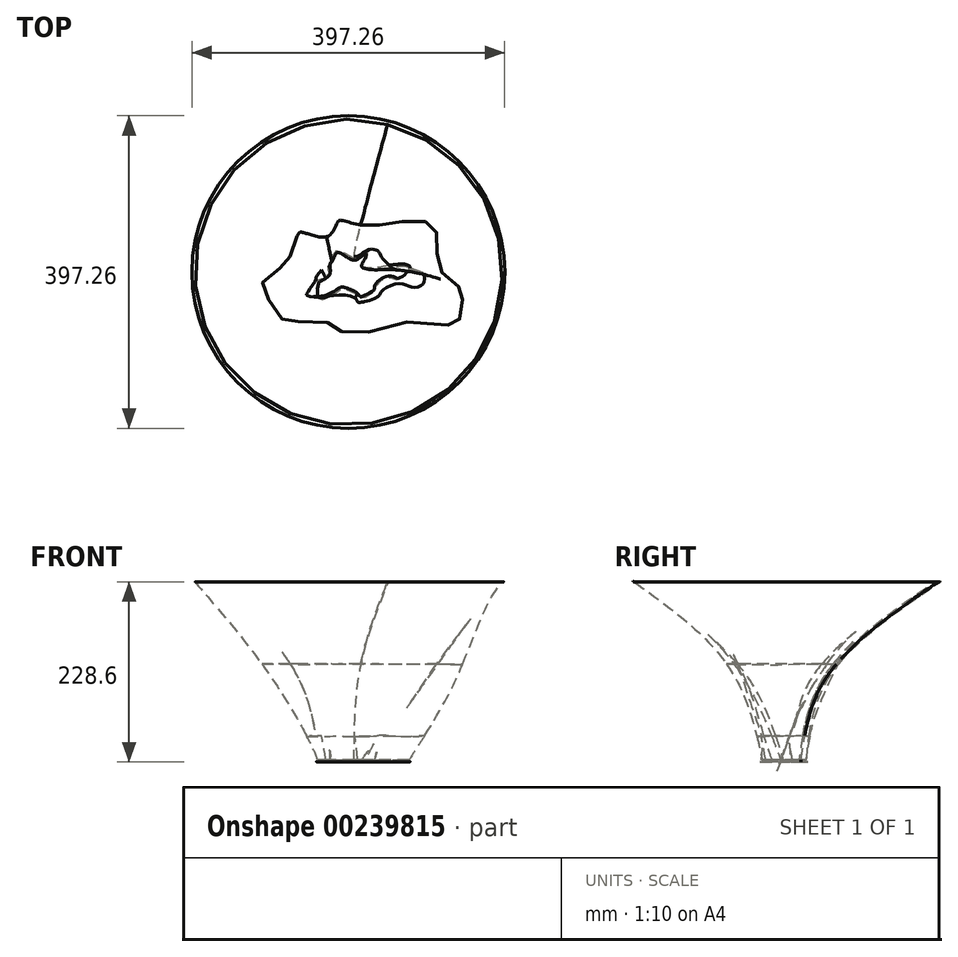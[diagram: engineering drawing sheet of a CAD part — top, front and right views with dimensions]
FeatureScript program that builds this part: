
annotation { "Feature Type Name" : "Feature", "Feature Type Description" : "" }
export const myFeature = defineFeature(function(context is Context, id is Id, definition is map)
    precondition{}
    {
        {
            var Q0;
            Q0=qCreatedBy(makeId("Top.planeOp"),FACE);
            var sketch = newSketch(context, id + "F0", { "sketchPlane" : qUnion([Q0])});
            skFitSpline(sketch, "E0", {"points": [v(14.79, 34.81) * mm, v(-29.61, 53.97) * mm, v(-52.04, 8.17) * mm, v(-46.44, 0) * mm, v(-67, -17.53) * mm, v(-77.75, -23.14) * mm, v(-80.55, -62.4) * mm, v(-67.47, -70.81) * mm, v(-22.6, -45.58) * mm, v(-13.72, -41.84) * mm, v(22.73, -59.6) * mm, v(26.94, -67.54) * mm, v(70.4, -45.1) * mm, v(70.4, -34.36) * mm, v(103.59, -13.33) * mm, v(124.62, -19.4) * mm, v(156.87, 8.17) * mm, v(145.18, 19.39) * mm, v(80.69, 12.38) * mm, v(69.47, 10.04) * mm, v(36.75, 13.31) * mm, v(39.1, 21.26) * mm, v(48.44, 46.96) * mm, v(40.5, 51.64) * mm, v(14.79, 34.81) * mm]});
            skSolve(sketch);
        }
        {
            var Q0;
            Q0=qCreatedBy(makeId("Top.planeOp"),FACE);
            cPlane(context, id + "F1", {"entities" : qUnion([Q0]), "cplaneType" : CPlaneType.OFFSET, "offset" : 203.2 * mm, "width" : 152.4 * mm, "height" : 152.4 * mm});
        }
        {
            var Q0;
            Q0=qCreatedBy(id+"F1.planeOp",FACE);
            var sketch = newSketch(context, id + "F2", { "sketchPlane" : qUnion([Q0])});
            skFitSpline(sketch, "E1", {"points": [v(-75.93, 66.67) * mm, v(-99.4, 77.65) * mm, v(-108.67, 75.44) * mm, v(-128.52, 20.74) * mm, v(-127.64, 13.68) * mm, v(-182.78, -22.93) * mm, v(-192.05, -50.28) * mm, v(-143.8, -107.42) * mm, v(-132.61, -116.25) * mm, v(-30.15, -110.36) * mm, v(-5.42, -128.03) * mm, v(81.14, -123.9) * mm, v(99.98, -113.9) * mm, v(165.93, -97.4) * mm, v(207.15, -107.42) * mm, v(262.5, -108) * mm, v(273.69, -92.1) * mm, v(273.1, -37.93) * mm, v(255.44, -20.27) * mm, v(201.26, 16.24) * mm, v(201.26, 52.75) * mm, v(190.07, 103.4) * mm, v(155.33, 113.4) * mm, v(78.2, 102.21) * mm, v(38.15, 91.61) * mm, v(-11.31, 102.8) * mm, v(-28.39, 102.8) * mm, v(-45.53, 66.34) * mm, v(-75.93, 66.67) * mm]});
            skSolve(sketch);
        }
        {
            var Q0;
            Q0=makeQuery(id+"F2.imprint","IMPRINT",FACE,{"disambiguationData":[TD([[makeQuery(id+"F2.imprint","IMPRINT",EDGE,{"derivedFrom":sQuery(id+"F2.wireOp",EDGE,"E1")}),1.0]])]});
            cPlane(context, id + "F3", {"entities" : qUnion([Q0]), "cplaneType" : CPlaneType.OFFSET, "offset" : 254 * mm, "width" : 152.4 * mm, "height" : 152.4 * mm});
        }
        {
            var Q0;
            Q0=qCreatedBy(id+"F3.planeOp",FACE);
            var sketch = newSketch(context, id + "F4", { "sketchPlane" : qUnion([Q0])});
            skCircle(sketch, "E2", {"center": v(0, 0) * mm, "radius": 397.27 * mm});
            skSolve(sketch);
        }
        {
            var Q0;
            Q0=makeQuery(id+"F0.imprint","IMPRINT",FACE,{"disambiguationData":[TD([[makeQuery(id+"F0.imprint","IMPRINT",EDGE,{"derivedFrom":sQuery(id+"F0.wireOp",EDGE,"E0")}),1.0]])]});
            var Q1;
            Q1=makeQuery(id+"F2.imprint","IMPRINT",FACE,{"disambiguationData":[TD([[makeQuery(id+"F2.imprint","IMPRINT",EDGE,{"derivedFrom":sQuery(id+"F2.wireOp",EDGE,"E1")}),1.0]])]});
            var Q2;
            Q2=makeQuery(id+"F4.imprint","IMPRINT",FACE,{"disambiguationData":[TD([[makeQuery(id+"F4.imprint","IMPRINT",EDGE,{"derivedFrom":sQuery(id+"F4.wireOp",EDGE,"E2")}),1.0]])]});
            loft(context, id + "F5", {"sheetProfilesArray" : [{ "sheetProfileEntities" : qUnion([Q0]) }, { "sheetProfileEntities" : qUnion([Q1]) }, { "sheetProfileEntities" : qUnion([Q2]) }]});
        }
        {
            var Q0;
            Q0=makeQuery(id+"F5.opLoft","CAP_FACE",FACE,{"disambiguationData":[OSD([makeQuery(id+"F4.imprint","IMPRINT",FACE,{"disambiguationData":[TD([[makeQuery(id+"F4.imprint","IMPRINT",EDGE,{"derivedFrom":sQuery(id+"F4.wireOp",EDGE,"E2")}),1.0]])]})])],"isStart":true});
            shell(context, id + "F6", {"entities" : qUnion([Q0]), "thickness" : 5.08 * mm});
        }
        {
            var Q0;
            Q0=makeQuery(id+"F5.opLoft","SWEPT_BODY",BODY,{"disambiguationData":[OSD([makeQuery(id+"F0.imprint","IMPRINT",FACE,{"disambiguationData":[TD([[makeQuery(id+"F0.imprint","IMPRINT",EDGE,{"derivedFrom":sQuery(id+"F0.wireOp",EDGE,"E0")}),1.0]])]}),sQuery(id+"F2.wireOp",EDGE,"E1"),makeQuery(id+"F4.imprint","IMPRINT",FACE,{"disambiguationData":[TD([[makeQuery(id+"F4.imprint","IMPRINT",EDGE,{"derivedFrom":sQuery(id+"F4.wireOp",EDGE,"E2")}),1.0]])]})])]});
            var Q1;
            Q1=qCreatedBy(makeId("Origin.pointOp"),VERTEX);
            transform(context, id + "F7", {"entities" : qUnion([Q0]), "transformType" : TransformType.SCALE_UNIFORMLY, "scale" : .5, "scalePoint" : qUnion([Q1]), "makeCopy" : false});
        }
    });
